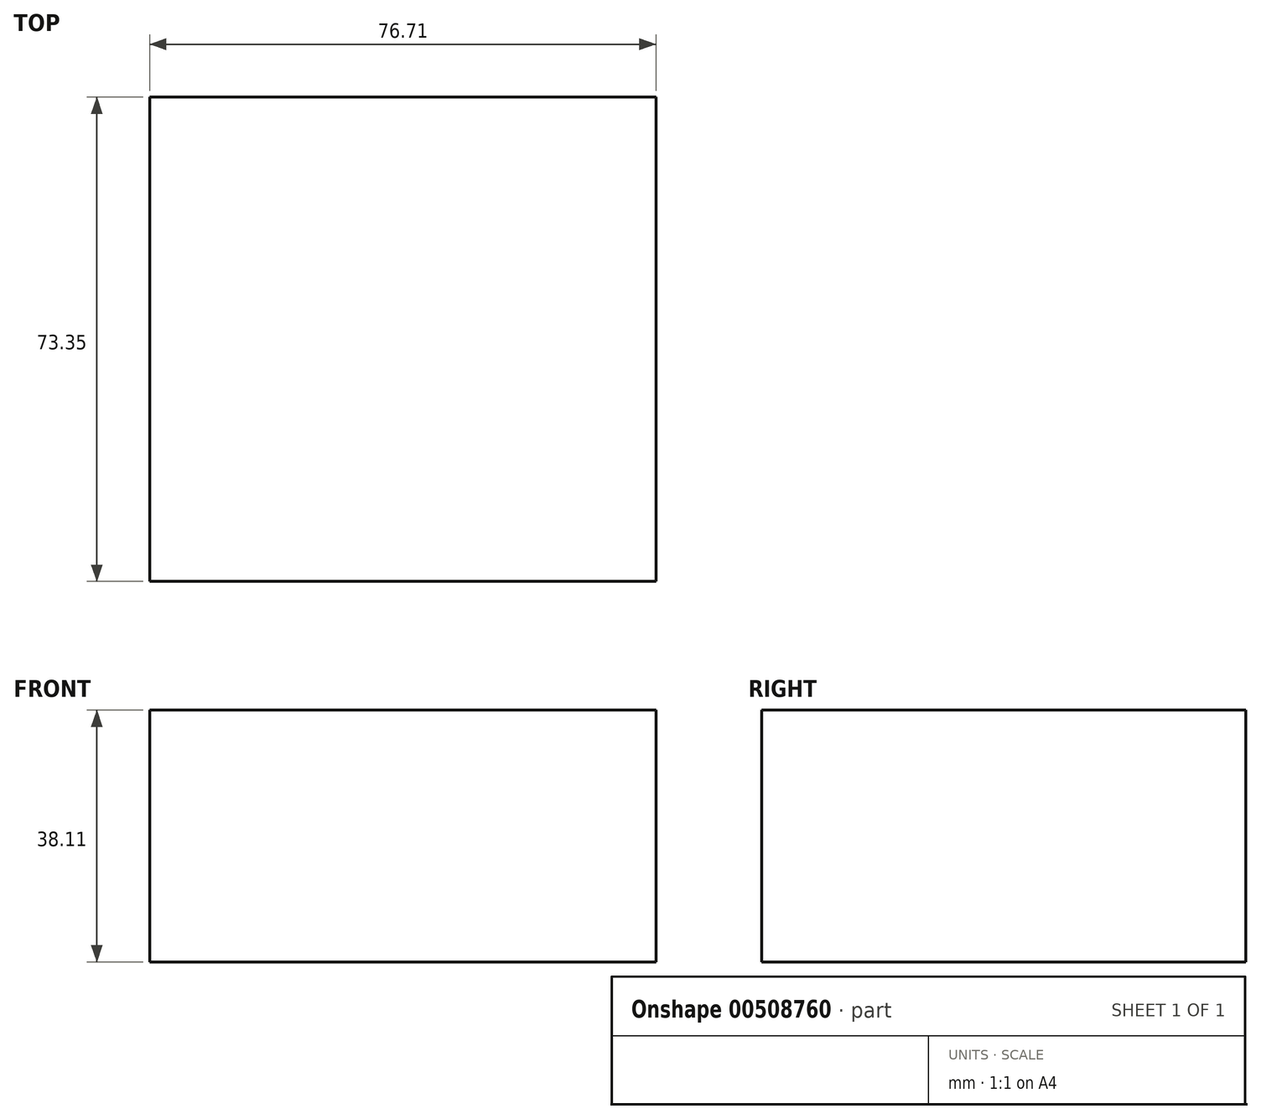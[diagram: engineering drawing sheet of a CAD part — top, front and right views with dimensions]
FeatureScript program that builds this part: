
annotation { "Feature Type Name" : "Feature", "Feature Type Description" : "" }
export const myFeature = defineFeature(function(context is Context, id is Id, definition is map)
    precondition{}
    {
        {
            var Q0;
            Q0=qCreatedBy(makeId("Front.planeOp"),FACE);
            var sketch = newSketch(context, id + "F0", { "sketchPlane" : qUnion([Q0])});
            skLineSegment(sketch, "E0.bottom", {"start": v(76.7, 0) * mm, "end": v(0, 0) * mm});
            skLineSegment(sketch, "E0.top", {"start": v(76.7, 38.11) * mm, "end": v(0, 38.11) * mm});
            skLineSegment(sketch, "E0.left", {"start": v(76.7, 0) * mm, "end": v(76.7, 38.11) * mm});
            skLineSegment(sketch, "E0.right", {"start": v(0, 0) * mm, "end": v(0, 38.11) * mm});
            skSolve(sketch);
        }
        {
            var Q0;
            Q0=makeQuery(id+"F0.imprint","IMPRINT",FACE,{"disambiguationData":[TD([[makeQuery(id+"F0.imprint","IMPRINT",EDGE,{"derivedFrom":sQuery(id+"F0.wireOp",EDGE,"E0.bottom")}),-1.0]])]});
            extrude(context, id + "F1", {"entities" : qUnion([Q0]), "depth" : 73.35 * mm});
        }
    });
